# Revit family: VIESSMANN - Vitocell 100-V (CVA.CVAA.CVAA-A) 160-950 L
name_source: partatom
category: Wyposażenie mechaniczne
revit_build: Autodesk Revit 2017 (Build: 20160720_1515(x64)
units: mm (PartAtom-declared; Revit-internal decimal feet)

## family parameters
Numer OmniClass = 23.65.35.11.11
Oparty na płaszczyźnie roboczej = Nie
Punkt obliczania pomieszczeń = Nie
Tnij formami wycięć po wczytaniu = Tak
Typ części = Normalny
Tytuł OmniClass = Storage Water Heaters
Współdzielony = Nie
Wymiar okrągłego złącza = Użyj średnicy
Zawsze pionowo = Tak

## types (6) — shared parameters
Autor = https://www.archispace.pl
Numer identyfikacyjny produktu = 9W241/11-13MC/E
Opis = Podgrzewacz pojemnościowy
Opis indeksowy = 9W241/11-13MC/E
Producent = Viessmann Sp.z.o.o.
Przepływ objętościowy wody grzewczej (dla podanych wydajności stałych) = 3.00 m³/h
Przepływ po stronie wody grzewczej = 3.00 m³/h
URL = https://www.viessmann-projektant.pl
Viessmann Kolor 1 = Viessmann Kolor 1
Viessmann Kolor 2 = Viessmann Kolor 2
Viessmann Kolor 3 = Viessmann Kolor 3

## per-type parameters (varying)
- Zbiornik CVAA-A/CVA 200L: Ciepła woda użytkowa=3/4"; Cyrkulacja=3/4"; Czas podgrzewu cwu przy tempraturze zasilania wodą grzewczą 70℃=37 min; Czas podgrzewu cwu przy tempraturze zasilania wodą grzewczą 80℃=24 min; Czas podgrzewu cwu przy tempraturze zasilania wodą grzewczą 90℃=19 min; Ilość ciepła dyżurnego=1.04/1.46 kWh/24h; Klasa efektywności energetycznej=A/B; Maks. ilość pobierana przy temperaturze na zasilaniu wodą grzewczą 70℃=25; Maks. ilość pobierana przy temperaturze na zasilaniu wodą grzewczą 80℃=25; Maks. ilość pobierana przy temperaturze na zasilaniu wodą grzewczą 90℃=26; Masa całkowita z izolacją cieplną=97.00 kg; Model=Podgrzewacz pojemnościowy Viessmann Vitocell 100-V CVAA-A/CVA 200L / Hot water storage tank Viessmann Vitocell 100-V CVAA-A/CVA 200L; Objętość brutto=205.5 L; Objętość wody grzewczej=5.5 L; Opory przepływu po stronie wody grzewczej=10500.0 Pa; Opory przepływu po stronie wody użytkowej=13000.0 Pa; Podział=581 mm  [stored 1.90617 ft]; Pojemność podgrzewacza=200.0 L; Powierzchnia grzewcza=1.0 m²; Powrót wody grzewczej=1"; Przepływ objętościowy wody grzewczej (przy podgrzewie cwu z 10 na 45℃) przy temperaturze na zasilaniu wodą grzewczą 50℃=0.22; Przepływ objętościowy wody grzewczej (przy podgrzewie cwu z 10 na 45℃) przy temperaturze na zasilaniu wodą grzewczą 60℃=0.42; Przepływ objętościowy wody grzewczej (przy podgrzewie cwu z 10 na 45℃) przy temperaturze na zasilaniu wodą grzewczą 70℃=0.61; Przepływ objętościowy wody grzewczej (przy podgrzewie cwu z 10 na 45℃) przy temperaturze na zasilaniu wodą grzewczą 80℃=0.79; Przepływ objętościowy wody grzewczej (przy podgrzewie cwu z 10 na 45℃) przy temperaturze na zasilaniu wodą grzewczą 90℃=0.98; Przepływ objętościowy wody grzewczej (przy podgrzewie cwu z 10 na 60℃) przy temperaturze na zasilaniu wodą grzewczą 70℃=0.33; Przepływ objętościowy wody grzewczej (przy podgrzewie cwu z 10 na 60℃) przy temperaturze na zasilaniu wodą grzewczą 80℃=0.48; Przepływ objętościowy wody grzewczej (przy podgrzewie cwu z 10 na 60℃) przy temperaturze na zasilaniu wodą grzewczą 90℃=0.62; Przepływ po stronie wody użytkowej=0.98 m³/h; Szerokość - bez izolacji cieplnej=0 mm  [stored 0 ft]; Szerokość - z izolacją cieplną=605 mm  [stored 1.98491 ft]; Współczynnik mocy NL przy temperaturze na zasilaniu wodą grzewczą 70℃=3.5; Współczynnik mocy NL przy temperaturze na zasilaniu wodą grzewczą 80℃=3.7; Współczynnik mocy NL przy temperaturze na zasilaniu wodą grzewczą 90℃=4; Wydajność krótkotrwała przy temperaturze na zasilaniu wodą grzewczą 70℃=246 L/10min; Wydajność krótkotrwała przy temperaturze na zasilaniu wodą grzewczą 80℃=252 L/10min; Wydajność krótkotrwała przy temperaturze na zasilaniu wodą grzewczą 90℃=262 L/10min; Wydajność stała (przy podgrzewie cwu z 10 na 45℃) i temperaturze na zasilaniu wodą grzewczą 50℃=9000; Wydajność stała (przy podgrzewie cwu z 10 na 45℃) i temperaturze na zasilaniu wodą grzewczą 60℃=17000; Wydajność stała (przy podgrzewie cwu z 10 na 45℃) i temperaturze na zasilaniu wodą grzewczą 70℃=25000; Wydajność stała (przy podgrzewie cwu z 10 na 45℃) i temperaturze na zasilaniu wodą grzewczą 80℃=32000; Wydajność stała (przy podgrzewie cwu z 10 na 45℃) i temperaturze na zasilaniu wodą grzewczą 90℃=40000; Wydajność stała (przy podgrzewie cwu z 10 na 60℃) i temperaturze na zasilaniu wodą grzewczą 70℃=19000; Wydajność stała (przy podgrzewie cwu z 10 na 60℃) i temperaturze na zasilaniu wodą grzewczą 80℃=28000; Wydajność stała (przy podgrzewie cwu z 10 na 60℃) i temperaturze na zasilaniu wodą grzewczą 90℃=36000; Wymiar przechylenia - bez izolacji cieplnej=0 mm  [stored 0 ft]; Wymiar przechylenia - z izolacją cieplną=1460 mm; Wysokośc montażu grzałki=333 mm  [stored 1.09252 ft]; Wysokośc powrotu wody grzewczej=249 mm  [stored 0.816929 ft]; Wysokość=1409 mm; Wysokość - bez izolacji cieplnej=0 mm  [stored 0 ft]; Wysokość - z izolacją cieplną=1409 mm; Wysokość króćca cwu=1270 mm; Wysokość króćca cyrkulacji=884 mm  [stored 2.90026 ft]; Wysokość króćca zasilania wodą grzewczą=634 mm  [stored 2.08005 ft]; Wysokość króćca zimna woda użytkowa=72 mm  [stored 0.23622 ft]; Występ króćców=317 mm  [stored 1.04003 ft]; Zasilanie wody grzewczej=1"; Zimna woda użytkowa=3/4"; Średnica - bez izolacji cieplnej=0 mm  [stored 0 ft]; Średnica - z izolacją cieplną=581 mm  [stored 1.90617 ft]; Średnica z izolacją cieplną=581 mm  [stored 1.90617 ft]
- Zbiornik CVAA-A/CVA 160L: Ciepła woda użytkowa=3/4"; Cyrkulacja=3/4"; Czas podgrzewu cwu przy tempraturze zasilania wodą grzewczą 70℃=34 min; Czas podgrzewu cwu przy tempraturze zasilania wodą grzewczą 80℃=24 min; Czas podgrzewu cwu przy tempraturze zasilania wodą grzewczą 90℃=19 min; Ilość ciepła dyżurnego=0.97/1.35 kWh/24h; Klasa efektywności energetycznej=A/B; Maks. ilość pobierana przy temperaturze na zasilaniu wodą grzewczą 70℃=20; Maks. ilość pobierana przy temperaturze na zasilaniu wodą grzewczą 80℃=21; Maks. ilość pobierana przy temperaturze na zasilaniu wodą grzewczą 90℃=21; Masa całkowita z izolacją cieplną=86.00 kg; Model=Podgrzewacz pojemnościowy Viessmann Vitocell 100-V CVAA-A/CVA 160L / Hot water storage tank Viessmann Vitocell 100-V CVAA-A/CVA 160L; Objętość brutto=165.5 L; Objętość wody grzewczej=5.5 L; Opory przepływu po stronie wody grzewczej=10500.0 Pa; Opory przepływu po stronie wody użytkowej=13000.0 Pa; Podział=581 mm  [stored 1.90617 ft]; Pojemność podgrzewacza=160.0 L; Powierzchnia grzewcza=1.0 m²; Powrót wody grzewczej=1"; Przepływ objętościowy wody grzewczej (przy podgrzewie cwu z 10 na 45℃) przy temperaturze na zasilaniu wodą grzewczą 50℃=0.22; Przepływ objętościowy wody grzewczej (przy podgrzewie cwu z 10 na 45℃) przy temperaturze na zasilaniu wodą grzewczą 60℃=0.42; Przepływ objętościowy wody grzewczej (przy podgrzewie cwu z 10 na 45℃) przy temperaturze na zasilaniu wodą grzewczą 70℃=0.61; Przepływ objętościowy wody grzewczej (przy podgrzewie cwu z 10 na 45℃) przy temperaturze na zasilaniu wodą grzewczą 80℃=0.79; Przepływ objętościowy wody grzewczej (przy podgrzewie cwu z 10 na 45℃) przy temperaturze na zasilaniu wodą grzewczą 90℃=0.98; Przepływ objętościowy wody grzewczej (przy podgrzewie cwu z 10 na 60℃) przy temperaturze na zasilaniu wodą grzewczą 70℃=0.33; Przepływ objętościowy wody grzewczej (przy podgrzewie cwu z 10 na 60℃) przy temperaturze na zasilaniu wodą grzewczą 80℃=0.48; Przepływ objętościowy wody grzewczej (przy podgrzewie cwu z 10 na 60℃) przy temperaturze na zasilaniu wodą grzewczą 90℃=0.62; Przepływ po stronie wody użytkowej=0.98 m³/h; Szerokość - bez izolacji cieplnej=0 mm  [stored 0 ft]; Szerokość - z izolacją cieplną=605 mm  [stored 1.98491 ft]; Współczynnik mocy NL przy temperaturze na zasilaniu wodą grzewczą 70℃=2.2; Współczynnik mocy NL przy temperaturze na zasilaniu wodą grzewczą 80℃=2.4; Współczynnik mocy NL przy temperaturze na zasilaniu wodą grzewczą 90℃=2.5; Wydajność krótkotrwała przy temperaturze na zasilaniu wodą grzewczą 70℃=199 L/10min; Wydajność krótkotrwała przy temperaturze na zasilaniu wodą grzewczą 80℃=207 L/10min; Wydajność krótkotrwała przy temperaturze na zasilaniu wodą grzewczą 90℃=210 L/10min; Wydajność stała (przy podgrzewie cwu z 10 na 45℃) i temperaturze na zasilaniu wodą grzewczą 50℃=9000; Wydajność stała (przy podgrzewie cwu z 10 na 45℃) i temperaturze na zasilaniu wodą grzewczą 60℃=17000; Wydajność stała (przy podgrzewie cwu z 10 na 45℃) i temperaturze na zasilaniu wodą grzewczą 70℃=25000; Wydajność stała (przy podgrzewie cwu z 10 na 45℃) i temperaturze na zasilaniu wodą grzewczą 80℃=32000; Wydajność stała (przy podgrzewie cwu z 10 na 45℃) i temperaturze na zasilaniu wodą grzewczą 90℃=40000; Wydajność stała (przy podgrzewie cwu z 10 na 60℃) i temperaturze na zasilaniu wodą grzewczą 70℃=19000; Wydajność stała (przy podgrzewie cwu z 10 na 60℃) i temperaturze na zasilaniu wodą grzewczą 80℃=28000; Wydajność stała (przy podgrzewie cwu z 10 na 60℃) i temperaturze na zasilaniu wodą grzewczą 90℃=36000; Wymiar przechylenia - bez izolacji cieplnej=0 mm  [stored 0 ft]; Wymiar przechylenia - z izolacją cieplną=1260 mm; Wysokośc montażu grzałki=333 mm  [stored 1.09252 ft]; Wysokośc powrotu wody grzewczej=249 mm  [stored 0.816929 ft]; Wysokość=1189 mm  [stored 3.90092 ft]; Wysokość - bez izolacji cieplnej=0 mm  [stored 0 ft]; Wysokość - z izolacją cieplną=1189 mm  [stored 3.90092 ft]; Wysokość króćca cwu=1050 mm  [stored 3.44488 ft]; Wysokość króćca cyrkulacji=884 mm  [stored 2.90026 ft]; Wysokość króćca zasilania wodą grzewczą=634 mm  [stored 2.08005 ft]; Wysokość króćca zimna woda użytkowa=72 mm  [stored 0.23622 ft]; Występ króćców=317 mm  [stored 1.04003 ft]; Zasilanie wody grzewczej=1"; Zimna woda użytkowa=3/4"; Średnica - bez izolacji cieplnej=0 mm  [stored 0 ft]; Średnica - z izolacją cieplną=581 mm  [stored 1.90617 ft]; Średnica z izolacją cieplną=581 mm  [stored 1.90617 ft]
- Zbiornik CVAA 950L: Ciepła woda użytkowa=1 1/4"; Cyrkulacja=1 1/4"; Czas podgrzewu cwu przy tempraturze zasilania wodą grzewczą 70℃=70 min; Czas podgrzewu cwu przy tempraturze zasilania wodą grzewczą 80℃=45 min; Czas podgrzewu cwu przy tempraturze zasilania wodą grzewczą 90℃=35 min; Ilość ciepła dyżurnego=2.48 kWh/24h; Maks. ilość pobierana przy temperaturze na zasilaniu wodą grzewczą 70℃=88; Maks. ilość pobierana przy temperaturze na zasilaniu wodą grzewczą 80℃=92; Maks. ilość pobierana przy temperaturze na zasilaniu wodą grzewczą 90℃=94; Masa całkowita z izolacją cieplną=363.00 kg; Model=Podgrzewacz pojemnościowy Viessmann Vitocell 100-V CVAA 950L / Hot water storage tank Viessmann Vitocell 100-V CVAA 950L; Objętość brutto=983.1 L; Objętość wody grzewczej=33.1 L; Opory przepływu po stronie wody grzewczej=7700.0 Pa; Opory przepływu po stronie wody użytkowej=25000.0 Pa; Podział=1062 mm  [stored 3.48425 ft]; Pojemność podgrzewacza=950.0 L; Powierzchnia grzewcza=3.9 m²; Powrót wody grzewczej=1 1/4"; Przepływ objętościowy wody grzewczej (przy podgrzewie cwu z 10 na 45℃) przy temperaturze na zasilaniu wodą grzewczą 50℃=0.87; Przepływ objętościowy wody grzewczej (przy podgrzewie cwu z 10 na 45℃) przy temperaturze na zasilaniu wodą grzewczą 60℃=1.43; Przepływ objętościowy wody grzewczej (przy podgrzewie cwu z 10 na 45℃) przy temperaturze na zasilaniu wodą grzewczą 70℃=1.93; Przepływ objętościowy wody grzewczej (przy podgrzewie cwu z 10 na 45℃) przy temperaturze na zasilaniu wodą grzewczą 80℃=2.40; Przepływ objętościowy wody grzewczej (przy podgrzewie cwu z 10 na 45℃) przy temperaturze na zasilaniu wodą grzewczą 90℃=2.86; Przepływ objętościowy wody grzewczej (przy podgrzewie cwu z 10 na 60℃) przy temperaturze na zasilaniu wodą grzewczą 70℃=1.00; Przepływ objętościowy wody grzewczej (przy podgrzewie cwu z 10 na 60℃) przy temperaturze na zasilaniu wodą grzewczą 80℃=1.38; Przepływ objętościowy wody grzewczej (przy podgrzewie cwu z 10 na 60℃) przy temperaturze na zasilaniu wodą grzewczą 90℃=1.73; Przepływ po stronie wody użytkowej=2.86 m³/h; Szerokość - bez izolacji cieplnej=1005 mm  [stored 3.29724 ft]; Szerokość - z izolacją cieplną=1110 mm  [stored 3.64173 ft]; Współczynnik mocy NL przy temperaturze na zasilaniu wodą grzewczą 70℃=39; Współczynnik mocy NL przy temperaturze na zasilaniu wodą grzewczą 80℃=42; Współczynnik mocy NL przy temperaturze na zasilaniu wodą grzewczą 90℃=44; Wydajność krótkotrwała przy temperaturze na zasilaniu wodą grzewczą 70℃=875 L/10min; Wydajność krótkotrwała przy temperaturze na zasilaniu wodą grzewczą 80℃=915 L/10min; Wydajność krótkotrwała przy temperaturze na zasilaniu wodą grzewczą 90℃=937 L/10min; Wydajność stała (przy podgrzewie cwu z 10 na 45℃) i temperaturze na zasilaniu wodą grzewczą 50℃=35000; Wydajność stała (przy podgrzewie cwu z 10 na 45℃) i temperaturze na zasilaniu wodą grzewczą 60℃=58000; Wydajność stała (przy podgrzewie cwu z 10 na 45℃) i temperaturze na zasilaniu wodą grzewczą 70℃=78000; Wydajność stała (przy podgrzewie cwu z 10 na 45℃) i temperaturze na zasilaniu wodą grzewczą 80℃=98000; Wydajność stała (przy podgrzewie cwu z 10 na 45℃) i temperaturze na zasilaniu wodą grzewczą 90℃=116000; Wydajność stała (przy podgrzewie cwu z 10 na 60℃) i temperaturze na zasilaniu wodą grzewczą 70℃=58000; Wydajność stała (przy podgrzewie cwu z 10 na 60℃) i temperaturze na zasilaniu wodą grzewczą 80℃=80000; Wydajność stała (przy podgrzewie cwu z 10 na 60℃) i temperaturze na zasilaniu wodą grzewczą 90℃=101000; Wymiar przechylenia - bez izolacji cieplnej=2286 mm; Wymiar przechylenia - z izolacją cieplną=0 mm  [stored 0 ft]; Wysokośc montażu grzałki=502 mm  [stored 1.64698 ft]; Wysokośc powrotu wody grzewczej=638 mm; Wysokość=2197 mm; Wysokość - bez izolacji cieplnej=2123 mm; Wysokość - z izolacją cieplną=2197 mm; Wysokość króćca cwu=2094 mm; Wysokość króćca cyrkulacji=1283 mm; Wysokość króćca zasilania wodą grzewczą=989 mm  [stored 3.24475 ft]; Wysokość króćca zimna woda użytkowa=79 mm; Występ króćców=555 mm  [stored 1.82087 ft]; Zasilanie wody grzewczej=1 1/4"; Zimna woda użytkowa=1 1/4"; Średnica - bez izolacji cieplnej=790 mm  [stored 2.59186 ft]; Średnica - z izolacją cieplną=1062 mm  [stored 3.48425 ft]; Średnica z izolacją cieplną=1062 mm  [stored 3.48425 ft]
- Zbiornik CVAA 300L: Ciepła woda użytkowa=1"; Cyrkulacja=1"; Czas podgrzewu cwu przy tempraturze zasilania wodą grzewczą 70℃=45 min; Czas podgrzewu cwu przy tempraturze zasilania wodą grzewczą 80℃=31 min; Czas podgrzewu cwu przy tempraturze zasilania wodą grzewczą 90℃=23 min; Ilość ciepła dyżurnego=1.65 kWh/24h; Klasa efektywności energetycznej=B; Maks. ilość pobierana przy temperaturze na zasilaniu wodą grzewczą 70℃=39; Maks. ilość pobierana przy temperaturze na zasilaniu wodą grzewczą 80℃=40; Maks. ilość pobierana przy temperaturze na zasilaniu wodą grzewczą 90℃=41; Masa całkowita z izolacją cieplną=156.00 kg; Model=Podgrzewacz pojemnościowy Viessmann Vitocell 100-V CVAA 300L / Hot water storage tank Viessmann Vitocell 100-V CVAA 300L; Objętość brutto=310.0 L; Objętość wody grzewczej=10.0 L; Opory przepływu po stronie wody grzewczej=18000.0 Pa; Opory przepływu po stronie wody użytkowej=7000.0 Pa; Podział=667 mm  [stored 2.18832 ft]; Pojemność podgrzewacza=300.0 L; Powierzchnia grzewcza=1.5 m²; Powrót wody grzewczej=1"; Przepływ objętościowy wody grzewczej (przy podgrzewie cwu z 10 na 45℃) przy temperaturze na zasilaniu wodą grzewczą 50℃=0.44; Przepływ objętościowy wody grzewczej (przy podgrzewie cwu z 10 na 45℃) przy temperaturze na zasilaniu wodą grzewczą 60℃=0.57; Przepływ objętościowy wody grzewczej (przy podgrzewie cwu z 10 na 45℃) przy temperaturze na zasilaniu wodą grzewczą 70℃=0.81; Przepływ objętościowy wody grzewczej (przy podgrzewie cwu z 10 na 45℃) przy temperaturze na zasilaniu wodą grzewczą 80℃=1.08; Przepływ objętościowy wody grzewczej (przy podgrzewie cwu z 10 na 45℃) przy temperaturze na zasilaniu wodą grzewczą 90℃=1.30; Przepływ objętościowy wody grzewczej (przy podgrzewie cwu z 10 na 60℃) przy temperaturze na zasilaniu wodą grzewczą 70℃=0.40; Przepływ objętościowy wody grzewczej (przy podgrzewie cwu z 10 na 60℃) przy temperaturze na zasilaniu wodą grzewczą 80℃=0.58; Przepływ objętościowy wody grzewczej (przy podgrzewie cwu z 10 na 60℃) przy temperaturze na zasilaniu wodą grzewczą 90℃=0.77; Przepływ po stronie wody użytkowej=1.30 m³/h; Szerokość - bez izolacji cieplnej=0 mm  [stored 0 ft]; Szerokość - z izolacją cieplną=744 mm  [stored 2.44094 ft]; Współczynnik mocy NL przy temperaturze na zasilaniu wodą grzewczą 70℃=8.7; Współczynnik mocy NL przy temperaturze na zasilaniu wodą grzewczą 80℃=9.3; Współczynnik mocy NL przy temperaturze na zasilaniu wodą grzewczą 90℃=9.7; Wydajność krótkotrwała przy temperaturze na zasilaniu wodą grzewczą 70℃=385 L/10min; Wydajność krótkotrwała przy temperaturze na zasilaniu wodą grzewczą 80℃=399 L/10min; Wydajność krótkotrwała przy temperaturze na zasilaniu wodą grzewczą 90℃=407 L/10min; Wydajność stała (przy podgrzewie cwu z 10 na 45℃) i temperaturze na zasilaniu wodą grzewczą 50℃=18000; Wydajność stała (przy podgrzewie cwu z 10 na 45℃) i temperaturze na zasilaniu wodą grzewczą 60℃=23000; Wydajność stała (przy podgrzewie cwu z 10 na 45℃) i temperaturze na zasilaniu wodą grzewczą 70℃=33000; Wydajność stała (przy podgrzewie cwu z 10 na 45℃) i temperaturze na zasilaniu wodą grzewczą 80℃=44000; Wydajność stała (przy podgrzewie cwu z 10 na 45℃) i temperaturze na zasilaniu wodą grzewczą 90℃=53000; Wydajność stała (przy podgrzewie cwu z 10 na 60℃) i temperaturze na zasilaniu wodą grzewczą 70℃=23000; Wydajność stała (przy podgrzewie cwu z 10 na 60℃) i temperaturze na zasilaniu wodą grzewczą 80℃=34000; Wydajność stała (przy podgrzewie cwu z 10 na 60℃) i temperaturze na zasilaniu wodą grzewczą 90℃=45000; Wymiar przechylenia - bez izolacji cieplnej=0 mm  [stored 0 ft]; Wymiar przechylenia - z izolacją cieplną=1825 mm; Wysokośc montażu grzałki=333 mm  [stored 1.09252 ft]; Wysokośc powrotu wody grzewczej=260 mm  [stored 0.853018 ft]; Wysokość=1734 mm; Wysokość - bez izolacji cieplnej=0 mm  [stored 0 ft]; Wysokość - z izolacją cieplną=1734 mm; Wysokość króćca cwu=1600 mm; Wysokość króćca cyrkulacji=1115 mm  [stored 3.65814 ft]; Wysokość króćca zasilania wodą grzewczą=875 mm  [stored 2.87073 ft]; Wysokość króćca zimna woda użytkowa=76 mm  [stored 0.249344 ft]; Występ króćców=361 mm  [stored 1.18438 ft]; Zasilanie wody grzewczej=1"; Zimna woda użytkowa=1"; Średnica - bez izolacji cieplnej=0 mm  [stored 0 ft]; Średnica - z izolacją cieplną=667 mm  [stored 2.18832 ft]; Średnica z izolacją cieplną=667 mm  [stored 2.18832 ft]
- Zbiornik CVA 500L: Ciepła woda użytkowa=1 1/4"; Cyrkulacja=1"; Czas podgrzewu cwu przy tempraturze zasilania wodą grzewczą 70℃=50 min; Czas podgrzewu cwu przy tempraturze zasilania wodą grzewczą 80℃=36 min; Czas podgrzewu cwu przy tempraturze zasilania wodą grzewczą 90℃=28 min; Ilość ciepła dyżurnego=1.95 kWh/24h; Klasa efektywności energetycznej=B; Maks. ilość pobierana przy temperaturze na zasilaniu wodą grzewczą 70℃=54; Maks. ilość pobierana przy temperaturze na zasilaniu wodą grzewczą 80℃=58; Maks. ilość pobierana przy temperaturze na zasilaniu wodą grzewczą 90℃=62; Masa całkowita z izolacją cieplną=181.00 kg; Model=Podgrzewacz pojemnościowy Viessmann Vitocell 100-V CVA 500L / Hot water storage tank Viessmann Vitocell 100-V CVA 500L; Objętość brutto=512.5 L; Objętość wody grzewczej=12.5 L; Opory przepływu po stronie wody grzewczej=21000.0 Pa; Opory przepływu po stronie wody użytkowej=8000.0 Pa; Podział=859 mm  [stored 2.81824 ft]; Pojemność podgrzewacza=500.0 L; Powierzchnia grzewcza=1.9 m²; Powrót wody grzewczej=1"; Przepływ objętościowy wody grzewczej (przy podgrzewie cwu z 10 na 45℃) przy temperaturze na zasilaniu wodą grzewczą 50℃=0.59; Przepływ objętościowy wody grzewczej (przy podgrzewie cwu z 10 na 45℃) przy temperaturze na zasilaniu wodą grzewczą 60℃=0.79; Przepływ objętościowy wody grzewczej (przy podgrzewie cwu z 10 na 45℃) przy temperaturze na zasilaniu wodą grzewczą 70℃=1.11; Przepływ objętościowy wody grzewczej (przy podgrzewie cwu z 10 na 45℃) przy temperaturze na zasilaniu wodą grzewczą 80℃=1.43; Przepływ objętościowy wody grzewczej (przy podgrzewie cwu z 10 na 45℃) przy temperaturze na zasilaniu wodą grzewczą 90℃=1.72; Przepływ objętościowy wody grzewczej (przy podgrzewie cwu z 10 na 60℃) przy temperaturze na zasilaniu wodą grzewczą 70℃=0.57; Przepływ objętościowy wody grzewczej (przy podgrzewie cwu z 10 na 60℃) przy temperaturze na zasilaniu wodą grzewczą 80℃=0.76; Przepływ objętościowy wody grzewczej (przy podgrzewie cwu z 10 na 60℃) przy temperaturze na zasilaniu wodą grzewczą 90℃=0.91; Przepływ po stronie wody użytkowej=1.72 m³/h; Szerokość - bez izolacji cieplnej=837 mm  [stored 2.74606 ft]; Szerokość - z izolacją cieplną=923 mm  [stored 3.02822 ft]; Współczynnik mocy NL przy temperaturze na zasilaniu wodą grzewczą 70℃=16.5; Współczynnik mocy NL przy temperaturze na zasilaniu wodą grzewczą 80℃=19; Współczynnik mocy NL przy temperaturze na zasilaniu wodą grzewczą 90℃=21; Wydajność krótkotrwała przy temperaturze na zasilaniu wodą grzewczą 70℃=540 L/10min; Wydajność krótkotrwała przy temperaturze na zasilaniu wodą grzewczą 80℃=583 L/10min; Wydajność krótkotrwała przy temperaturze na zasilaniu wodą grzewczą 90℃=618 L/10min; Wydajność stała (przy podgrzewie cwu z 10 na 45℃) i temperaturze na zasilaniu wodą grzewczą 50℃=24000; Wydajność stała (przy podgrzewie cwu z 10 na 45℃) i temperaturze na zasilaniu wodą grzewczą 60℃=32000; Wydajność stała (przy podgrzewie cwu z 10 na 45℃) i temperaturze na zasilaniu wodą grzewczą 70℃=45000; Wydajność stała (przy podgrzewie cwu z 10 na 45℃) i temperaturze na zasilaniu wodą grzewczą 80℃=58000; Wydajność stała (przy podgrzewie cwu z 10 na 45℃) i temperaturze na zasilaniu wodą grzewczą 90℃=70000; Wydajność stała (przy podgrzewie cwu z 10 na 60℃) i temperaturze na zasilaniu wodą grzewczą 70℃=33000; Wydajność stała (przy podgrzewie cwu z 10 na 60℃) i temperaturze na zasilaniu wodą grzewczą 80℃=44000; Wydajność stała (przy podgrzewie cwu z 10 na 60℃) i temperaturze na zasilaniu wodą grzewczą 90℃=53000; Wymiar przechylenia - bez izolacji cieplnej=1860 mm; Wymiar przechylenia - z izolacją cieplną=0 mm  [stored 0 ft]; Wysokośc montażu grzałki=422 mm  [stored 1.38451 ft]; Wysokośc powrotu wody grzewczej=638 mm; Wysokość=1948 mm; Wysokość - bez izolacji cieplnej=1844 mm; Wysokość - z izolacją cieplną=1948 mm; Wysokość króćca cwu=1784 mm; Wysokość króćca cyrkulacji=1230 mm  [stored 4.03543 ft]; Wysokość króćca zasilania wodą grzewczą=924 mm  [stored 3.0315 ft]; Wysokość króćca zimna woda użytkowa=107 mm  [stored 0.35105 ft]; Występ króćców=455 mm; Zasilanie wody grzewczej=1"; Zimna woda użytkowa=1 1/4"; Średnica - bez izolacji cieplnej=650 mm  [stored 2.13255 ft]; Średnica - z izolacją cieplną=859 mm  [stored 2.81824 ft]; Średnica z izolacją cieplną=859 mm  [stored 2.81824 ft]
- Zbiornik CVAA 750L: Ciepła woda użytkowa=1 1/4"; Cyrkulacja=1 1/4"; Czas podgrzewu cwu przy tempraturze zasilania wodą grzewczą 70℃=45 min; Czas podgrzewu cwu przy tempraturze zasilania wodą grzewczą 80℃=31 min; Czas podgrzewu cwu przy tempraturze zasilania wodą grzewczą 90℃=23 min; Ilość ciepła dyżurnego=2.28 kWh/24h; Maks. ilość pobierana przy temperaturze na zasilaniu wodą grzewczą 70℃=67; Maks. ilość pobierana przy temperaturze na zasilaniu wodą grzewczą 80℃=77; Maks. ilość pobierana przy temperaturze na zasilaniu wodą grzewczą 90℃=85; Masa całkowita z izolacją cieplną=301.00 kg; Model=Podgrzewacz pojemnościowy Viessmann Vitocell 100-V CVAA 750L / Hot water storage tank Viessmann Vitocell 100-V CVAA 750L; Objętość brutto=779.7 L; Objętość wody grzewczej=29.7 L; Opory przepływu po stronie wody grzewczej=7700.0 Pa; Opory przepływu po stronie wody użytkowej=20000.0 Pa; Podział=1062 mm  [stored 3.48425 ft]; Pojemność podgrzewacza=750.0 L; Powierzchnia grzewcza=3.5 m²; Powrót wody grzewczej=1 1/4"; Przepływ objętościowy wody grzewczej (przy podgrzewie cwu z 10 na 45℃) przy temperaturze na zasilaniu wodą grzewczą 50℃=0.81; Przepływ objętościowy wody grzewczej (przy podgrzewie cwu z 10 na 45℃) przy temperaturze na zasilaniu wodą grzewczą 60℃=1.33; Przepływ objętościowy wody grzewczej (przy podgrzewie cwu z 10 na 45℃) przy temperaturze na zasilaniu wodą grzewczą 70℃=1.79; Przepływ objętościowy wody grzewczej (przy podgrzewie cwu z 10 na 45℃) przy temperaturze na zasilaniu wodą grzewczą 80℃=2.24; Przepływ objętościowy wody grzewczej (przy podgrzewie cwu z 10 na 45℃) przy temperaturze na zasilaniu wodą grzewczą 90℃=2.67; Przepływ objętościowy wody grzewczej (przy podgrzewie cwu z 10 na 60℃) przy temperaturze na zasilaniu wodą grzewczą 70℃=0.92; Przepływ objętościowy wody grzewczej (przy podgrzewie cwu z 10 na 60℃) przy temperaturze na zasilaniu wodą grzewczą 80℃=1.28; Przepływ objętościowy wody grzewczej (przy podgrzewie cwu z 10 na 60℃) przy temperaturze na zasilaniu wodą grzewczą 90℃=1.61; Przepływ po stronie wody użytkowej=2.67 m³/h; Szerokość - bez izolacji cieplnej=1005 mm  [stored 3.29724 ft]; Szerokość - z izolacją cieplną=1110 mm  [stored 3.64173 ft]; Współczynnik mocy NL przy temperaturze na zasilaniu wodą grzewczą 70℃=25; Współczynnik mocy NL przy temperaturze na zasilaniu wodą grzewczą 80℃=32; Współczynnik mocy NL przy temperaturze na zasilaniu wodą grzewczą 90℃=38; Wydajność krótkotrwała przy temperaturze na zasilaniu wodą grzewczą 70℃=665 L/10min; Wydajność krótkotrwała przy temperaturze na zasilaniu wodą grzewczą 80℃=770 L/10min; Wydajność krótkotrwała przy temperaturze na zasilaniu wodą grzewczą 90℃=850 L/10min; Wydajność stała (przy podgrzewie cwu z 10 na 45℃) i temperaturze na zasilaniu wodą grzewczą 50℃=33000; Wydajność stała (przy podgrzewie cwu z 10 na 45℃) i temperaturze na zasilaniu wodą grzewczą 60℃=54000; Wydajność stała (przy podgrzewie cwu z 10 na 45℃) i temperaturze na zasilaniu wodą grzewczą 70℃=73000; Wydajność stała (przy podgrzewie cwu z 10 na 45℃) i temperaturze na zasilaniu wodą grzewczą 80℃=91000; Wydajność stała (przy podgrzewie cwu z 10 na 45℃) i temperaturze na zasilaniu wodą grzewczą 90℃=109000; Wydajność stała (przy podgrzewie cwu z 10 na 60℃) i temperaturze na zasilaniu wodą grzewczą 70℃=54000; Wydajność stała (przy podgrzewie cwu z 10 na 60℃) i temperaturze na zasilaniu wodą grzewczą 80℃=75000; Wydajność stała (przy podgrzewie cwu z 10 na 60℃) i temperaturze na zasilaniu wodą grzewczą 90℃=94000; Wymiar przechylenia - bez izolacji cieplnej=1980 mm; Wymiar przechylenia - z izolacją cieplną=0 mm  [stored 0 ft]; Wysokośc montażu grzałki=513 mm  [stored 1.68307 ft]; Wysokośc powrotu wody grzewczej=377 mm  [stored 1.23688 ft]; Wysokość=1897 mm; Wysokość - bez izolacji cieplnej=1817 mm; Wysokość - z izolacją cieplną=1897 mm; Wysokość króćca cwu=1788 mm; Wysokość króćca cyrkulacji=1179 mm  [stored 3.86811 ft]; Wysokość króćca zasilania wodą grzewczą=916 mm; Wysokość króćca zimna woda użytkowa=79 mm; Występ króćców=555 mm  [stored 1.82087 ft]; Zasilanie wody grzewczej=1 1/4"; Zimna woda użytkowa=1 1/4"; Średnica - bez izolacji cieplnej=790 mm  [stored 2.59186 ft]; Średnica - z izolacją cieplną=1062 mm  [stored 3.48425 ft]; Średnica z izolacją cieplną=1062 mm  [stored 3.48425 ft]

note: source unit labels omitted for Maks. ilość pobierana przy temperaturze na zasilaniu wodą grzewczą 70℃, Maks. ilość pobierana przy temperaturze na zasilaniu wodą grzewczą 80℃, Maks. ilość pobierana przy temperaturze na zasilaniu wodą grzewczą 90℃, Przepływ objętościowy wody grzewczej (przy podgrzewie cwu z 10 na 45℃) przy temperaturze na zasilaniu wodą grzewczą 50℃, Przepływ objętościowy wody grzewczej (przy podgrzewie cwu z 10 na 45℃) przy temperaturze na zasilaniu wodą grzewczą 60℃, Przepływ objętościowy wody grzewczej (przy podgrzewie cwu z 10 na 45℃) przy temperaturze na zasilaniu wodą grzewczą 70℃, Przepływ objętościowy wody grzewczej (przy podgrzewie cwu z 10 na 45℃) przy temperaturze na zasilaniu wodą grzewczą 80℃, Przepływ objętościowy wody grzewczej (przy podgrzewie cwu z 10 na 45℃) przy temperaturze na zasilaniu wodą grzewczą 90℃, Przepływ objętościowy wody grzewczej (przy podgrzewie cwu z 10 na 60℃) przy temperaturze na zasilaniu wodą grzewczą 70℃, Przepływ objętościowy wody grzewczej (przy podgrzewie cwu z 10 na 60℃) przy temperaturze na zasilaniu wodą grzewczą 80℃, Przepływ objętościowy wody grzewczej (przy podgrzewie cwu z 10 na 60℃) przy temperaturze na zasilaniu wodą grzewczą 90℃, Wydajność stała (przy podgrzewie cwu z 10 na 45℃) i temperaturze na zasilaniu wodą grzewczą 50℃, Wydajność stała (przy podgrzewie cwu z 10 na 45℃) i temperaturze na zasilaniu wodą grzewczą 60℃, Wydajność stała (przy podgrzewie cwu z 10 na 45℃) i temperaturze na zasilaniu wodą grzewczą 70℃, Wydajność stała (przy podgrzewie cwu z 10 na 45℃) i temperaturze na zasilaniu wodą grzewczą 80℃, Wydajność stała (przy podgrzewie cwu z 10 na 45℃) i temperaturze na zasilaniu wodą grzewczą 90℃, Wydajność stała (przy podgrzewie cwu z 10 na 60℃) i temperaturze na zasilaniu wodą grzewczą 70℃, Wydajność stała (przy podgrzewie cwu z 10 na 60℃) i temperaturze na zasilaniu wodą grzewczą 80℃, Wydajność stała (przy podgrzewie cwu z 10 na 60℃) i temperaturze na zasilaniu wodą grzewczą 90℃ — the stored unit's dimension contradicts the parameter name (converter mislabeling)

note: [stored X ft] marks values corroborated as IEEE doubles in the binary element streams (Revit-internal decimal feet)
